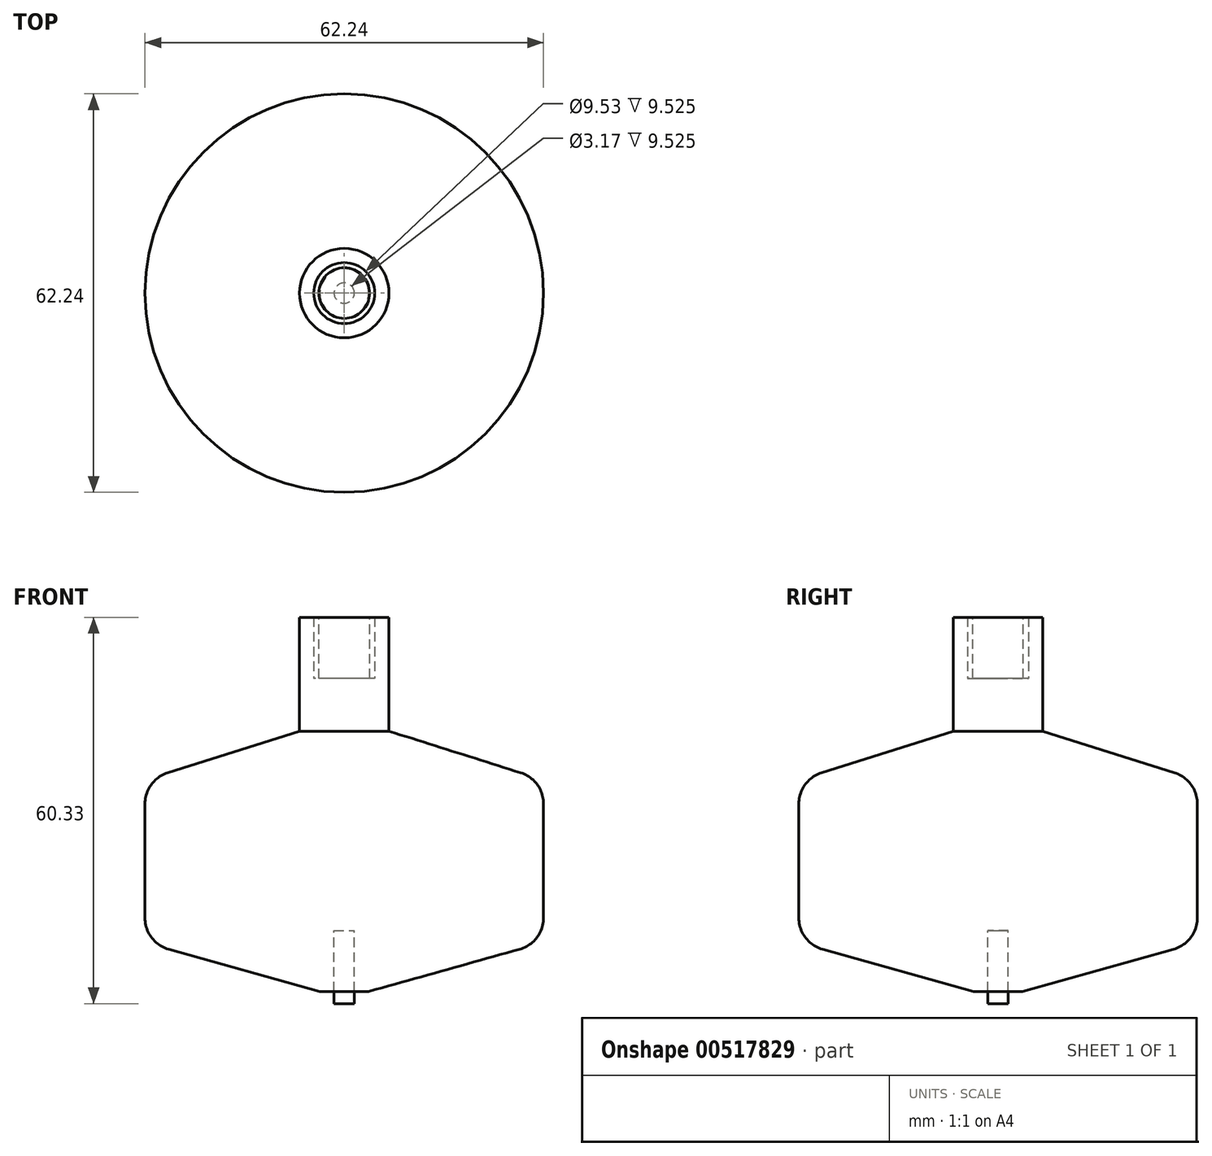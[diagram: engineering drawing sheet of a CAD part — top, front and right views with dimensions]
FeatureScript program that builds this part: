
annotation { "Feature Type Name" : "Feature", "Feature Type Description" : "" }
export const myFeature = defineFeature(function(context is Context, id is Id, definition is map)
    precondition{}
    {
        {
            var Q0;
            Q0=qCreatedBy(makeId("Front.planeOp"),FACE);
            var sketch = newSketch(context, id + "F0", { "sketchPlane" : qUnion([Q0])});
            skLineSegment(sketch, "E0", {"start": v(31.12, 12.07) * mm, "end": v(31.12, 37.47) * mm});
            skLineSegment(sketch, "E1", {"start": v(6.99, 62.87) * mm, "end": v(0, 62.87) * mm});
            skLineSegment(sketch, "E2", {"start": v(0, 62.87) * mm, "end": v(0, 4.45) * mm});
            skLineSegment(sketch, "E3", {"start": v(0, 4.45) * mm, "end": v(3.81, 4.45) * mm});
            skLineSegment(sketch, "E4", {"start": v(3.81, 4.45) * mm, "end": v(31.12, 12.07) * mm});
            skLineSegment(sketch, "E5", {"start": v(31.12, 37.47) * mm, "end": v(6.99, 45.09) * mm});
            skLineSegment(sketch, "E6", {"start": v(6.99, 45.09) * mm, "end": v(6.99, 62.87) * mm});
            skPoint(sketch, "E7", {"position": v(31.12, 24.77) * mm});
            skSolve(sketch);
        }
        {
            var Q0;
            Q0=makeQuery(id+"F0.imprint","IMPRINT",FACE,{"disambiguationData":[TD([[makeQuery(id+"F0.imprint","IMPRINT",EDGE,{"derivedFrom":sQuery(id+"F0.wireOp",EDGE,"E0")}),1.0]])]});
            var Q1;
            Q1=sQuery(id+"F0.wireOp",EDGE,"E2");
            revolve(context, id + "F1", {"entities" : qUnion([Q0]), "axis" : qUnion([Q1]), "revolveType" : RevolveType.FULL});
        }
        {
            var Q0;
            Q0=makeQuery(id+"F1.opRevolve","SWEPT_FACE",FACE,{"disambiguationData":[OSD([sQuery(id+"F0.wireOp",EDGE,"E1")])]});
            var sketch = newSketch(context, id + "F2", { "sketchPlane" : qUnion([Q0])});
            skCircle(sketch, "E8", {"center": v(0, 0) * mm, "radius": 4.76 * mm});
            skSolve(sketch);
        }
        {
            var Q0;
            Q0=makeQuery(id+"F2.imprint","IMPRINT",FACE,{"disambiguationData":[TD([[makeQuery(id+"F2.imprint","IMPRINT",EDGE,{"derivedFrom":sQuery(id+"F2.wireOp",EDGE,"E8")}),1.0]])]});
            extrude(context, id + "F3", {"entities" : qUnion([Q0]), "operationType" : NewBodyOperationType.REMOVE, "oppositeDirection" : true, "depth" : 9.52 * mm});
        }
        {
            var Q0;
            Q0=makeQuery(id+"F1.opRevolve","SWEPT_FACE",FACE,{"disambiguationData":[OSD([sQuery(id+"F0.wireOp",EDGE,"E3")])]});
            var sketch = newSketch(context, id + "F4", { "sketchPlane" : qUnion([Q0])});
            skCircle(sketch, "E9", {"center": v(0, 0) * mm, "radius": 1.59 * mm});
            skSolve(sketch);
        }
        {
            var Q0;
            Q0=qSketchRegion(id+"F4",true);
            extrude(context, id + "F5", {"entities" : qUnion([Q0]), "operationType" : NewBodyOperationType.REMOVE, "oppositeDirection" : true, "depth" : 9.52 * mm, "offsetDistance" : 25.4 * mm});
        }
        {
            var Q0;
            Q0=makeQuery(id+"F3.boolean.opBoolean","COPY",FACE,{"derivedFrom":makeQuery(id+"F3.opExtrude","CAP_FACE",FACE,{"disambiguationData":[OSD([sQuery(id+"F2.wireOp",EDGE,"E8")])],"isStart":false})});
            extrude(context, id + "F6", {"entities" : qUnion([Q0]), "depth" : 9.52 * mm});
        }
        {
            var Q0;
            Q0=makeQuery(id+"F6.opExtrude","CAP_FACE",FACE,{"disambiguationData":[OSD([sQuery(id+"F2.wireOp",EDGE,"E8")])],"isStart":false});
            var sketch = newSketch(context, id + "F7", { "sketchPlane" : qUnion([Q0])});
            skCircle(sketch, "E10", {"center": v(0, 0) * mm, "radius": 3.95 * mm});
            skSolve(sketch);
        }
        {
            var Q0;
            Q0=makeQuery(id+"F7.imprint","IMPRINT",FACE,{"disambiguationData":[TD([[makeQuery(id+"F7.imprint","IMPRINT",EDGE,{"derivedFrom":sQuery(id+"F7.wireOp",EDGE,"E10")}),1.0]])]});
            extrude(context, id + "F8", {"entities" : qUnion([Q0]), "operationType" : NewBodyOperationType.REMOVE, "oppositeDirection" : true, "depth" : 9.52 * mm});
        }
        {
            var Q0;
            Q0=makeQuery(id+"F5.boolean.opBoolean","COPY",FACE,{"derivedFrom":makeQuery(id+"F5.opExtrude","CAP_FACE",FACE,{"disambiguationData":[OSD([sQuery(id+"F4.wireOp",EDGE,"E9")])],"isStart":false})});
            extrude(context, id + "F9", {"entities" : qUnion([Q0]), "depth" : 11.43 * mm});
        }
        {
            var Q0;
            Q0=makeQuery(id+"F1.opRevolve","SWEPT_FACE",FACE,{"disambiguationData":[OSD([sQuery(id+"F0.wireOp",EDGE,"E0")])]});
            fillet(context, id + "F10", {"entities" : qUnion([Q0]), "radius" : 5.08 * mm, "tangentPropagation" : true, "allowEdgeOverflow" : false});
        }
    });
